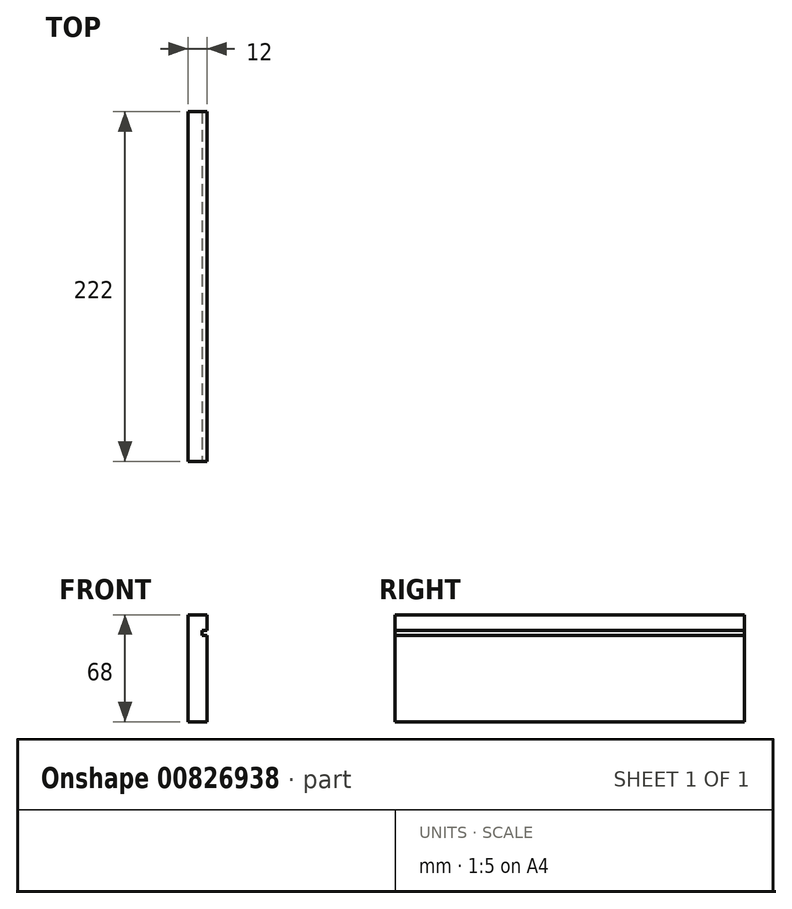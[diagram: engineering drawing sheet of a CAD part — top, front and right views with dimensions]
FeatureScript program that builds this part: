
annotation { "Feature Type Name" : "Feature", "Feature Type Description" : "" }
export const myFeature = defineFeature(function(context is Context, id is Id, definition is map)
    precondition{}
    {
        {
            var Q0;
            Q0=qCreatedBy(makeId("Right.planeOp"),FACE);
            var sketch = newSketch(context, id + "F0", { "sketchPlane" : qUnion([Q0])});
            skLineSegment(sketch, "E0.bottom", {"start": v(111, 34) * mm, "end": v(-111, 34) * mm});
            skLineSegment(sketch, "E0.top", {"start": v(111, -34) * mm, "end": v(-111, -34) * mm});
            skLineSegment(sketch, "E0.left", {"start": v(111, 34) * mm, "end": v(111, -34) * mm});
            skLineSegment(sketch, "E0.right", {"start": v(-111, 34) * mm, "end": v(-111, -34) * mm});
            skPoint(sketch, "E0.middle", {"position": v(0, 0) * mm});
            skSolve(sketch);
        }
        {
            var Q0;
            Q0=makeQuery(id+"F0.imprint","IMPRINT",FACE,{"disambiguationData":[TD([[makeQuery(id+"F0.imprint","IMPRINT",EDGE,{"derivedFrom":sQuery(id+"F0.wireOp",EDGE,"E0.bottom")}),1.0]])]});
            extrude(context, id + "F1", {"entities" : qUnion([Q0]), "depth" : 12 * mm, "offsetDistance" : 25.4 * mm});
        }
        {
            var Q0;
            Q0=makeQuery(id+"F1.opExtrude","SWEPT_FACE",FACE,{"disambiguationData":[OSD([sQuery(id+"F0.wireOp",EDGE,"E0.right")])]});
            var sketch = newSketch(context, id + "F2", { "sketchPlane" : qUnion([Q0])});
            skLineSegment(sketch, "E1.bottom", {"start": v(12, 24) * mm, "end": v(9, 24) * mm});
            skLineSegment(sketch, "E1.top", {"start": v(12, 21) * mm, "end": v(9, 21) * mm});
            skLineSegment(sketch, "E1.left", {"start": v(12, 24) * mm, "end": v(12, 21) * mm});
            skLineSegment(sketch, "E1.right", {"start": v(9, 24) * mm, "end": v(9, 21) * mm});
            skSolve(sketch);
        }
        {
            var Q0;
            Q0 = qSketchRegion(id + "F2", true);
            extrude(context, id + "F3", {"entities" : qUnion([Q0]), "operationType" : NewBodyOperationType.REMOVE, "oppositeDirection" : true, "depth" : 31343.6 * mm, "offsetDistance" : 25.4 * mm});
        }
    });
